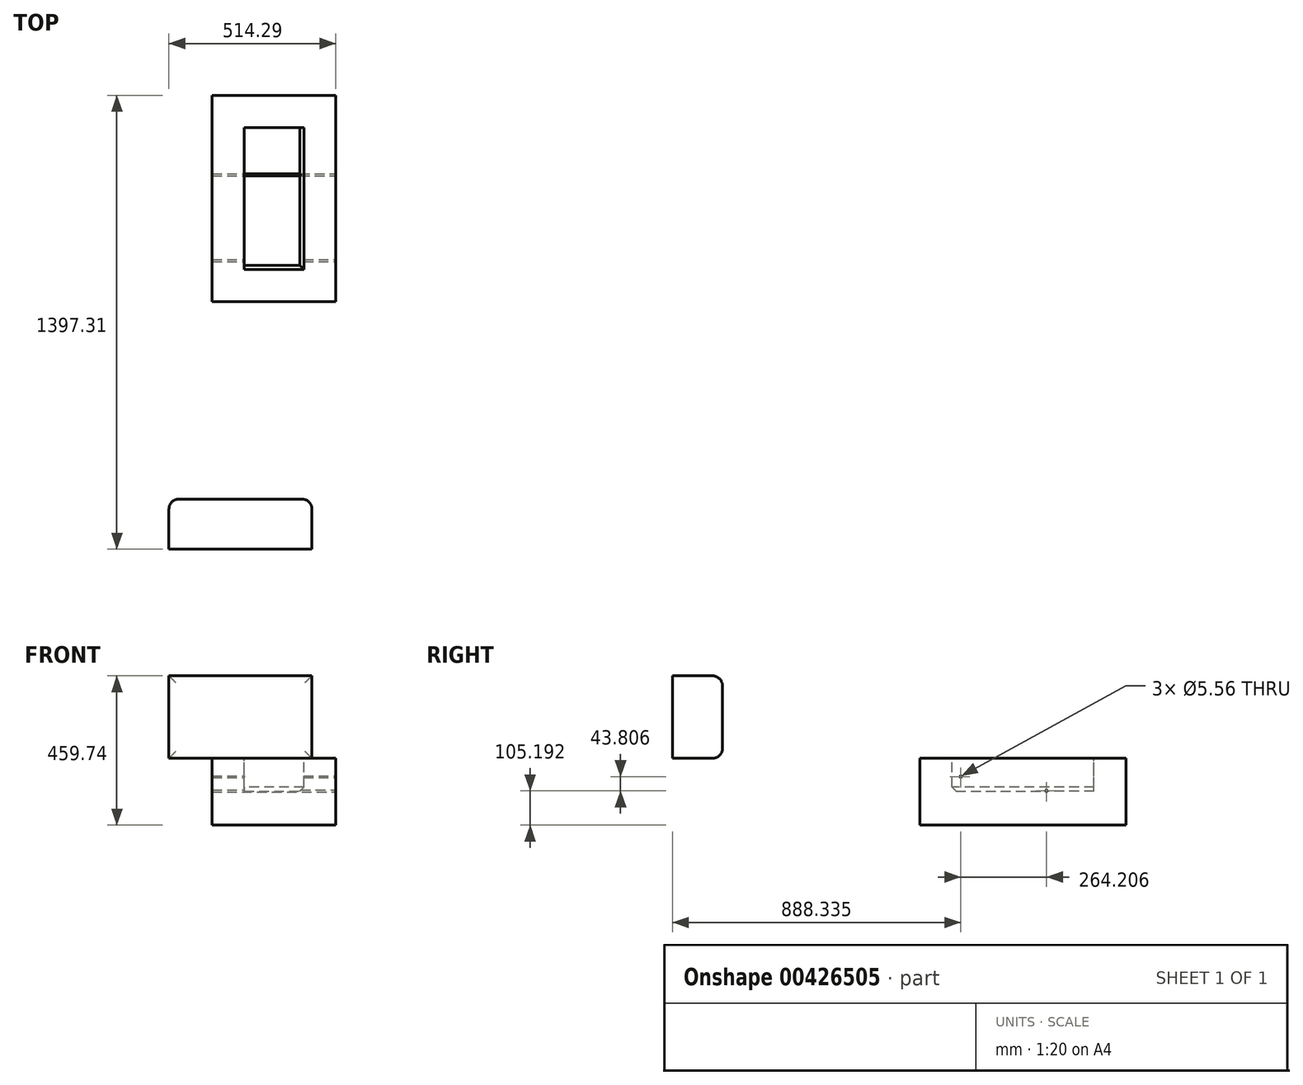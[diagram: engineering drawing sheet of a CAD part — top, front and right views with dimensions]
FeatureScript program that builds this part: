
annotation { "Feature Type Name" : "Feature", "Feature Type Description" : "" }
export const myFeature = defineFeature(function(context is Context, id is Id, definition is map)
    precondition{}
    {
        {
            var Q0;
            Q0=qCreatedBy(makeId("Top.planeOp"),FACE);
            var sketch = newSketch(context, id + "F0", { "sketchPlane" : qUnion([Q0])});
            skLineSegment(sketch, "E0.bottom", {"start": v(190.5, -317.5) * mm, "end": v(-190.5, -317.5) * mm});
            skLineSegment(sketch, "E0.top", {"start": v(190.5, 317.5) * mm, "end": v(-190.5, 317.5) * mm});
            skLineSegment(sketch, "E0.left", {"start": v(190.5, -317.5) * mm, "end": v(190.5, 317.5) * mm});
            skLineSegment(sketch, "E0.right", {"start": v(-190.5, -317.5) * mm, "end": v(-190.5, 317.5) * mm});
            skPoint(sketch, "E0.middle", {"position": v(0, 0) * mm});
            skSolve(sketch);
        }
        {
            var Q0;
            Q0 = qSketchRegion(id + "F0", true);
            extrude(context, id + "F1", {"entities" : qUnion([Q0]), "depth" : 205.74 * mm});
        }
        {
            var Q0;
            Q0=makeQuery(id+"F1.opExtrude","CAP_FACE",FACE,{"disambiguationData":[OSD([sQuery(id+"F0.wireOp",EDGE,"E0.bottom"),sQuery(id+"F0.wireOp",EDGE,"E0.top"),sQuery(id+"F0.wireOp",EDGE,"E0.left"),sQuery(id+"F0.wireOp",EDGE,"E0.right")])],"isStart":false});
            var sketch = newSketch(context, id + "F2", { "sketchPlane" : qUnion([Q0])});
            skLineSegment(sketch, "E1.0", {"start": v(91.7, -218.7) * mm, "end": v(91.7, 218.7) * mm});
            skLineSegment(sketch, "E1.1", {"start": v(-91.7, -218.7) * mm, "end": v(91.7, -218.7) * mm});
            skLineSegment(sketch, "E1.2", {"start": v(-91.7, 218.7) * mm, "end": v(-91.7, -218.7) * mm});
            skLineSegment(sketch, "E1.3", {"start": v(91.7, 218.7) * mm, "end": v(-91.7, 218.7) * mm});
            skSolve(sketch);
        }
        {
            var Q0;
            Q0 = qSketchRegion(id + "F2", true);
            extrude(context, id + "F3", {"entities" : qUnion([Q0]), "operationType" : NewBodyOperationType.REMOVE, "oppositeDirection" : true, "depth" : 101.1 * mm});
        }
        {
            var Q0;
            Q0=makeQuery(id+"F1.opExtrude","CAP_FACE",FACE,{"disambiguationData":[OSD([sQuery(id+"F0.wireOp",EDGE,"E0.bottom"),sQuery(id+"F0.wireOp",EDGE,"E0.top"),sQuery(id+"F0.wireOp",EDGE,"E0.left"),sQuery(id+"F0.wireOp",EDGE,"E0.right")])],"isStart":false});
            var sketch = newSketch(context, id + "F4", { "sketchPlane" : qUnion([Q0])});
            skLineSegment(sketch, "E2.bottom", {"start": v(-323.8, -1079.81) * mm, "end": v(116.5, -1079.81) * mm});
            skLineSegment(sketch, "E2.top", {"start": v(-323.8, -925.73) * mm, "end": v(116.5, -925.73) * mm});
            skLineSegment(sketch, "E2.left", {"start": v(-323.8, -1079.81) * mm, "end": v(-323.8, -925.73) * mm});
            skLineSegment(sketch, "E2.right", {"start": v(116.5, -1079.81) * mm, "end": v(116.5, -925.73) * mm});
            skSolve(sketch);
        }
        {
            var Q0;
            Q0 = qSketchRegion(id + "F4", true);
            extrude(context, id + "F5", {"entities" : qUnion([Q0]), "depth" : 254 * mm});
        }
        {
            var Q0;
            Q0=makeQuery(id+"F5.opExtrude","SWEPT_FACE",FACE,{"disambiguationData":[OSD([sQuery(id+"F4.wireOp",EDGE,"E2.top")])]});
            fillet(context, id + "F6", {"entities" : qUnion([Q0]), "radius" : 30.66 * mm, "tangentPropagation" : true, "allowEdgeOverflow" : false});
        }
        {
            var Q0;
            Q0=makeQuery(id+"F3.boolean.opBoolean","COPY",EDGE,{"derivedFrom":makeQuery(id+"F3.opExtrude","CAP_EDGE",EDGE,{"disambiguationData":[OSD([sQuery(id+"F2.wireOp",EDGE,"E1.1")])],"isStart":false})});
            var Q1;
            Q1=makeQuery(id+"F3.boolean.opBoolean","COPY",EDGE,{"derivedFrom":makeQuery(id+"F3.opExtrude","CAP_EDGE",EDGE,{"disambiguationData":[OSD([sQuery(id+"F2.wireOp",EDGE,"E1.0")])],"isStart":false})});
            chamfer(context, id + "F7", {"entities" : qUnion([Q0, Q1]), "width" : 12.7 * mm, "tangentPropagation" : true});
        }
        {
            var Q0;
            Q0=makeQuery(id+"F1.opExtrude","SWEPT_FACE",FACE,{"disambiguationData":[OSD([sQuery(id+"F0.wireOp",EDGE,"E0.left")])]});
            var sketch = newSketch(context, id + "F8", { "sketchPlane" : qUnion([Q0])});
            skPoint(sketch, "E3", {"position": v(-191.47, 149) * mm});
            skPoint(sketch, "E4", {"position": v(72.73, 105.2) * mm});
            skSolve(sketch);
        }
        {
            var Q0;
            Q0=sQuery(id+"F8.wireOp",VERTEX,"E3");
            var Q1;
            Q1=sQuery(id+"F8.wireOp",VERTEX,"E4");
            var Q2;
            Q2=makeQuery(id+"F1.opExtrude","SWEPT_BODY",BODY,{"disambiguationData":[OSD([sQuery(id+"F0.wireOp",EDGE,"E0.bottom"),sQuery(id+"F0.wireOp",EDGE,"E0.top"),sQuery(id+"F0.wireOp",EDGE,"E0.left"),sQuery(id+"F0.wireOp",EDGE,"E0.right")])]});
            hole(context, id + "F9", {"style" : HoleStyle.SIMPLE, "endStyle" : HoleEndStyle.THROUGH, "standardTappedOrClearance" : lookupTablePath({ "standard" : "ANSI", "engagement" : "50%", "pitch" : "20 tpi", "size" : "1/4", "type" : "Tapped" }), "standardBlindInLast" : lookupTablePath({ "standard" : "ANSI", "engagement" : "50%", "pitch" : "20 tpi", "size" : "1/4", "type" : "Tapped" }), "holeDiameter" : 5.56 * mm, "showTappedDepth" : true, "isTappedThrough" : true, "tappedDepth" : 12.7 * mm, "tapClearance" : 3, "locations" : qUnion([Q0, Q1]), "scope" : qUnion([Q2]), "majorDiameter" : 6.35 * mm});
        }
    });
